# Revit family: Reece_Vanity_Kado_Neue_All Doors and Drawers
name_source: partatom
category: Casework
revit_build: Autodesk Revit 2018 (Build: 20190510_1515(x64)
units: mm (PartAtom-declared; Revit-internal decimal feet)

## family parameters
Always vertical = Yes
Cut with Voids When Loaded = Yes
Room Calculation Point = Yes
Shared = Yes
Work Plane-Based = Yes

## types (1)
- Reece_All types
    Default Elevation = 0 mm  [stored 0 ft]
    Description = -
    Disclaimer = THIS FILE IS THE PROPERTY OF THE REECE GROUP. IT MAY NOT BE REPRODUCED, REVERSE-ENGINEERED OR MODIFIED. ANY REPUBLICATION, TRANSMISSION OR DISTRIBUTION FOR THE PURPOSE OF COMMERCIALLY EXPLOITING THE FILES IS PROHIBITED.
    Finish = Please refer to Colour, Finish and Material Variations Document for more information.
    Keynote = Product #, Reece_Vanity_Kado_Neue_All Doors and Drawers - Reece_All types
    Manufacturer = Kado
    Model = Neue
    Reece_Bowl_Offset = 0 mm  [stored 0 ft]
    Reece_Cabinet_Height Dimension = 400 mm  [stored 1.31234 ft]
    Reece_Centre Panel_Offset = 504 mm  [stored 1.65354 ft]
    Reece_Detail_Additional = Please refer to Colour, Finish and Material Variations Document for more information.
    Reece_Detail_Disclaimer = THIS FILE IS THE PROPERTY OF THE REECE GROUP. IT MAY NOT BE REPRODUCED, REVERSE-ENGINEERED OR MODIFIED. ANY REPUBLICATION, TRANSMISSION OR DISTRIBUTION FOR THE PURPOSE OF COMMERCIALLY EXPLOITING THE FILES IS PROHIBITED.
    Reece_Door_160 mm_Hammer Handle = No
    Reece_Door_60 mm_Blaze Handle = No
    Reece_Door_Gap = 3 mm  [stored 0.00984252 ft]
    Reece_Drawer_160 mm_Hammer Handle = No
    Reece_Drawer_350 mm_ Blaze Handle = No
    Reece_Drawer_Plumbing Cut_Left = 1 mm  [stored 0.00328084 ft]
    Reece_Drawer_Plumbing Cut_Right = 1 mm  [stored 0.00328084 ft]
    Reece_Drawer_Side Cut_1 = 17 mm
    Reece_Drawer_Side Cut_2 = 17 mm
    Reece_Material_Benchtop = Reece_Caesarstone_Pure White
    Reece_Material_Cabinet = Reece_Polyurethane_Milton Moon Grey
    Reece_Material_Handle = Reece_Brass_Matte Black
    Reece_Panel_Offset = 504 mm  [stored 1.65354 ft]
    Reece_Panel_Switch = No
    Reece_Panel_Thickness_Top = 20 mm  [stored 0.0656168 ft]
    Reece_Product_Brand = Kado
    Reece_Product_Mount = Wall Mounted
    Reece_Product_Sub Brand = Neue
    Reece_Product_Type = Vanity
    Reece_Product_Web Page = https://www.reece.com.au
    Reece_Vanity_Bowl_Centre = Yes
    Reece_Vanity_Bowl_Count = 1
    Reece_Vanity_Bowl_Left = No
    Reece_Vanity_Bowl_Right = No
    Reece_Vanity_Doors = No
    Reece_Vanity_Drawers = No
    Reece_Vanity_Drawers_Centre Void = No
    Reece_Vanity_Drawers_Cut = Yes
    Reece_Vanity_Single_Drawer = No
    Reece_Vanity_Top_Depth = 500 mm  [stored 1.64042 ft]
    Reece_Vanity_Top_Width = 1500 mm  [stored 4.92126 ft]
    Reece_Vertical_Division_Count = 2
    Type Comments = Vanity
    URL = https://www.reece.com.au

note: [stored X ft] marks values corroborated as IEEE doubles in the binary element streams (Revit-internal decimal feet)

## geometry (parser evidence)
native form markers: Sweep x14
no freeform markers — native parametric forms only
